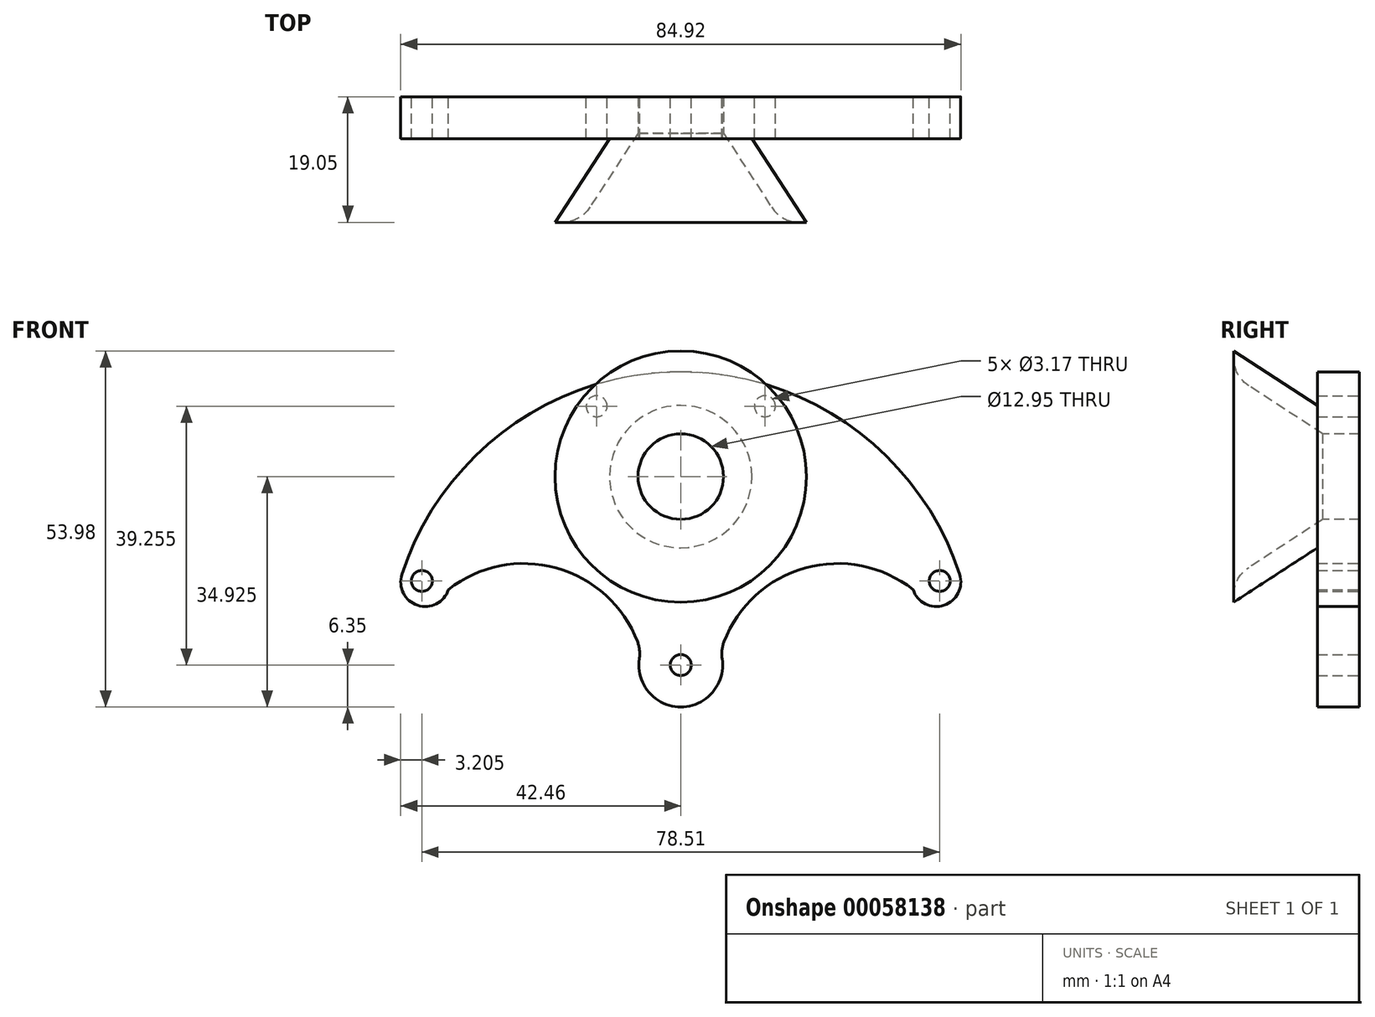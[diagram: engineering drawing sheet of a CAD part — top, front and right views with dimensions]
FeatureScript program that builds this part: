
annotation { "Feature Type Name" : "Feature", "Feature Type Description" : "" }
export const myFeature = defineFeature(function(context is Context, id is Id, definition is map)
    precondition{}
    {
        {
            var Q0;
            Q0=qCreatedBy(makeId("Front.planeOp"),FACE);
            var sketch = newSketch(context, id + "F0", { "sketchPlane" : qUnion([Q0])});
            skArc(sketch, "E0", {"start": v(42.27, 13.74) * mm, "mid": v(0, 44.45) * mm, "end": v(-42.27, 13.74) * mm});
            skCircle(sketch, "E1", {"center": v(0, 0) * mm, "radius": 41.28 * mm, "construction": true});
            skLineSegment(sketch, "E2", {"start": v(0, 0) * mm, "end": v(66.09, 21.47) * mm, "construction": true});
            skLineSegment(sketch, "E3", {"start": v(0, 0) * mm, "end": v(-65, 21.12) * mm, "construction": true});
            skCircle(sketch, "E4", {"center": v(-39.25, 12.75) * mm, "radius": 1.59 * mm});
            skCircle(sketch, "E5", {"center": v(39.25, 12.75) * mm, "radius": 1.59 * mm});
            skCircle(sketch, "E6", {"center": v(0, 0) * mm, "radius": 1.59 * mm});
            skLineSegment(sketch, "E7", {"start": v(0, 0) * mm, "end": v(-23.3, 71.72) * mm, "construction": true});
            skLineSegment(sketch, "E8", {"start": v(0, 0) * mm, "end": v(23.74, 73.06) * mm, "construction": true});
            skCircle(sketch, "E9", {"center": v(-12.75, 39.25) * mm, "radius": 1.59 * mm});
            skCircle(sketch, "E10", {"center": v(12.75, 39.25) * mm, "radius": 1.59 * mm});
            skCircle(sketch, "E11", {"center": v(0, 0) * mm, "radius": 25.4 * mm, "construction": true});
            skPoint(sketch, "E12", {"position": v(-42.27, 13.74) * mm});
            skPoint(sketch, "E13", {"position": v(42.27, 13.74) * mm});
            skArc(sketch, "E14", {"start": v(-6.04, 1.96) * mm, "mid": v(0, -6.35) * mm, "end": v(6.04, 1.96) * mm});
            skArc(sketch, "E15", {"start": v(-42.27, 13.74) * mm, "mid": v(-39.9, 9.06) * mm, "end": v(-35.22, 11.44) * mm});
            skArc(sketch, "E16", {"start": v(-6.04, 1.96) * mm, "mid": v(-18.1, 14.5) * mm, "end": v(-35.22, 11.44) * mm});
            skArc(sketch, "E17.MirrorCS", {"start": v(42.27, 13.74) * mm, "mid": v(39.9, 9.06) * mm, "end": v(35.22, 11.44) * mm});
            skArc(sketch, "E18.MirrorCS", {"start": v(6.04, 1.96) * mm, "mid": v(18.1, 14.5) * mm, "end": v(35.22, 11.44) * mm});
            skSolve(sketch);
        }
        {
            var Q0;
            Q0 = qSketchRegion(id + "F0", true);
            extrude(context, id + "F1", {"entities" : qUnion([Q0]), "depth" : 6.35 * mm});
        }
        {
            var Q0;
            Q0=makeQuery(id+"F1.opExtrude","CAP_FACE",FACE,{"disambiguationData":[OSD([sQuery(id+"F0.wireOp",EDGE,"E0"),sQuery(id+"F0.wireOp",EDGE,"E4"),sQuery(id+"F0.wireOp",EDGE,"E5"),sQuery(id+"F0.wireOp",EDGE,"E6"),sQuery(id+"F0.wireOp",EDGE,"E9"),sQuery(id+"F0.wireOp",EDGE,"E10"),sQuery(id+"F0.wireOp",EDGE,"E14"),sQuery(id+"F0.wireOp",EDGE,"E15"),sQuery(id+"F0.wireOp",EDGE,"E16"),sQuery(id+"F0.wireOp",EDGE,"E17.MirrorCS"),sQuery(id+"F0.wireOp",EDGE,"E18.MirrorCS")])],"isStart":false});
            var sketch = newSketch(context, id + "F2", { "sketchPlane" : qUnion([Q0])});
            skCircle(sketch, "E19", {"center": v(0, 0) * mm, "radius": 28.58 * mm, "construction": true});
            skCircle(sketch, "E20", {"center": v(0, 28.58) * mm, "radius": 10.8 * mm});
            skSolve(sketch);
        }
        {
            var Q0;
            Q0=qCreatedBy(makeId("Front.planeOp"),FACE);
            cPlane(context, id + "F3", {"entities" : qUnion([Q0]), "cplaneType" : CPlaneType.OFFSET, "offset" : 19.05 * mm, "width" : 152.4 * mm, "height" : 152.4 * mm});
        }
        {
            var Q0;
            Q0=qCreatedBy(id+"F3.planeOp",FACE);
            var sketch = newSketch(context, id + "F4", { "sketchPlane" : qUnion([Q0])});
            skCircle(sketch, "E21", {"center": v(0, 28.58) * mm, "radius": 19.05 * mm});
            skSolve(sketch);
        }
        {
            var Q1;
            Q1=makeQuery(id+"F2.imprint","IMPRINT",FACE,{"disambiguationData":[TD([[makeQuery(id+"F2.imprint","IMPRINT",EDGE,{"derivedFrom":sQuery(id+"F2.wireOp",EDGE,"E20")}),1.0]])]});
            var Q2;
            Q2=makeQuery(id+"F4.imprint","IMPRINT",FACE,{"disambiguationData":[TD([[makeQuery(id+"F4.imprint","IMPRINT",EDGE,{"derivedFrom":sQuery(id+"F4.wireOp",EDGE,"E21")}),1.0]])]});
            loft(context, id + "F5", {"operationType" : NewBodyOperationType.ADD, "sheetProfilesArray" : [{ "sheetProfileEntities" : qUnion([Q1]) }, { "sheetProfileEntities" : qUnion([Q2]) }]});
        }
        {
            var Q0;
            Q0=makeQuery(id+"F5.opLoft","CAP_FACE",FACE,{"disambiguationData":[OSD([makeQuery(id+"F4.imprint","IMPRINT",FACE,{"disambiguationData":[TD([[makeQuery(id+"F4.imprint","IMPRINT",EDGE,{"derivedFrom":sQuery(id+"F4.wireOp",EDGE,"E21")}),1.0]])]})])],"isStart":true});
            shell(context, id + "F6", {"entities" : qUnion([Q0]), "thickness" : 3.17 * mm});
        }
        {
            var Q0;
            Q0=makeQuery(id+"F5.opLoft","CAP_FACE",FACE,{"disambiguationData":[OSD([makeQuery(id+"F4.imprint","IMPRINT",FACE,{"disambiguationData":[TD([[makeQuery(id+"F4.imprint","IMPRINT",EDGE,{"derivedFrom":sQuery(id+"F4.wireOp",EDGE,"E21")}),1.0]])]})])],"isStart":true});
            var sketch = newSketch(context, id + "F7", { "sketchPlane" : qUnion([Q0])});
            skCircle(sketch, "E22", {"center": v(0, 28.58) * mm, "radius": 6.48 * mm});
            skSolve(sketch);
        }
        {
            var Q0;
            Q0 = qSketchRegion(id + "F7", true);
            extrude(context, id + "F8", {"entities" : qUnion([Q0]), "operationType" : NewBodyOperationType.REMOVE, "endBound" : BoundingType.THROUGH_ALL, "oppositeDirection" : true, "depth" : 25.4 * mm});
        }
        {
            var Q0;
            Q0=makeQuery(id+"F6.opShell","OFFSET_EDGE",EDGE,{"disambiguationData":[OSD([sQuery(id+"F2.wireOp",EDGE,"E20"),sQuery(id+"F4.wireOp",EDGE,"E21")])]});
            fillet(context, id + "F9", {"entities" : qUnion([Q0]), "radius" : 5.08 * mm, "tangentPropagation" : true, "allowEdgeOverflow" : false});
        }
        {
            var Q0;
            Q0=makeQuery(id+"F1.opExtrude","SWEPT_EDGE",EDGE,{"disambiguationData":[OSD([sQuery(id+"F0.wireOp",EDGE,"E14"),sQuery(id+"F0.wireOp",EDGE,"E16")])]});
            var Q1;
            Q1=makeQuery(id+"F1.opExtrude","SWEPT_EDGE",EDGE,{"disambiguationData":[OSD([sQuery(id+"F0.wireOp",EDGE,"E14"),sQuery(id+"F0.wireOp",EDGE,"E18.MirrorCS")])]});
            fillet(context, id + "F10", {"entities" : qUnion([Q0, Q1]), "radius" : 5.08 * mm, "tangentPropagation" : true, "allowEdgeOverflow" : false});
        }
    });
